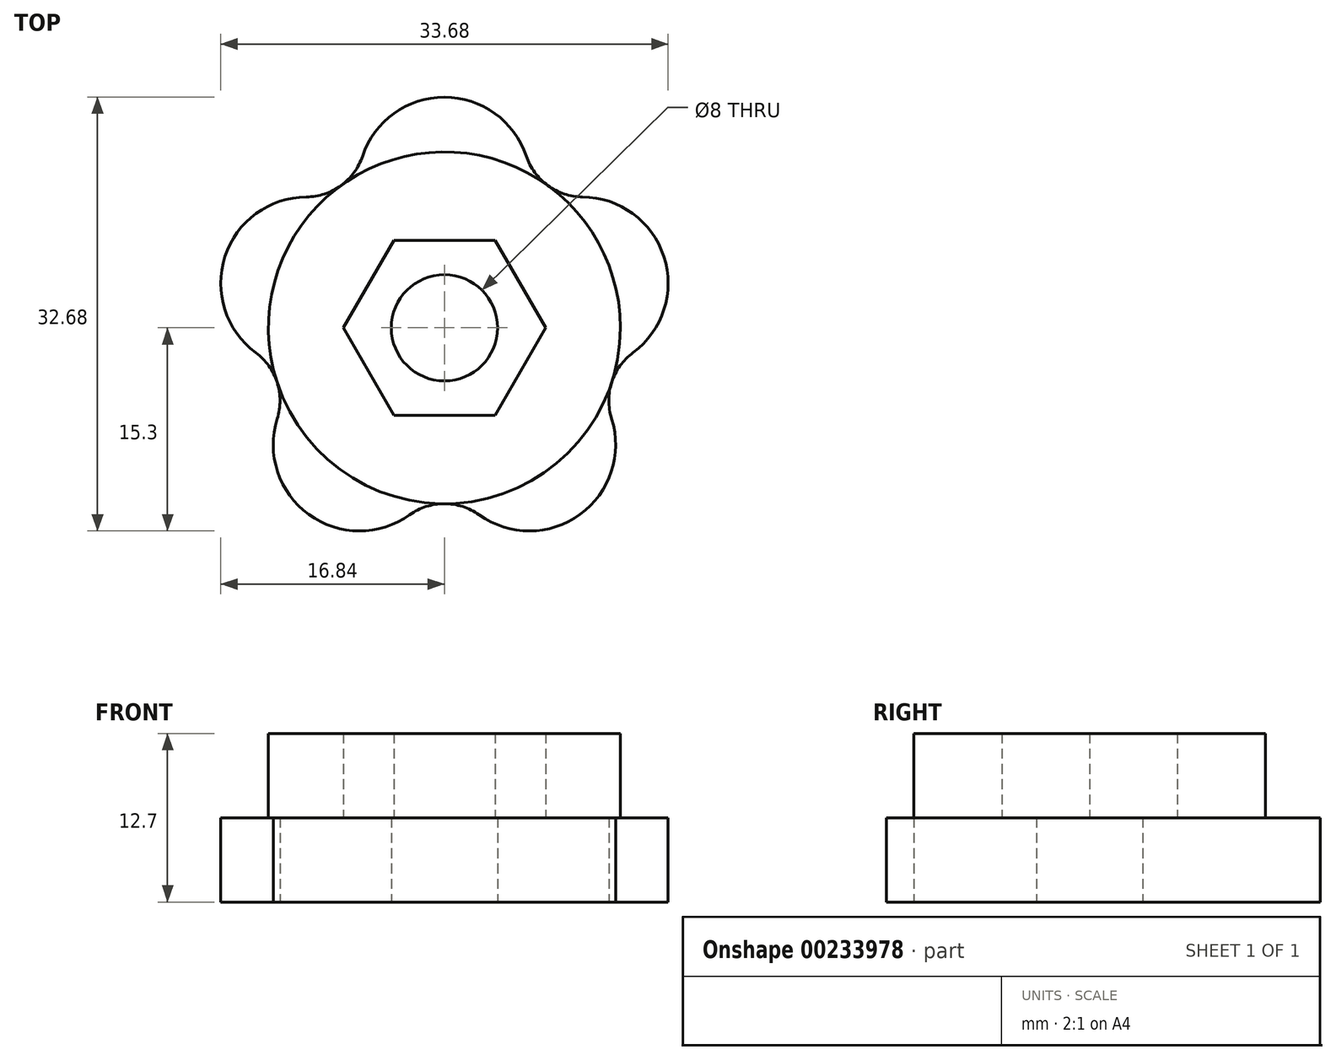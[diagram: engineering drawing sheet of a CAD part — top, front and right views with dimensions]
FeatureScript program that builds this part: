
annotation { "Feature Type Name" : "Feature", "Feature Type Description" : "" }
export const myFeature = defineFeature(function(context is Context, id is Id, definition is map)
    precondition{}
    {
        {
            var Q0;
            Q0=qCreatedBy(makeId("Top.planeOp"),FACE);
            var sketch = newSketch(context, id + "F0", { "sketchPlane" : qUnion([Q0])});
            skCircle(sketch, "E0", {"center": v(0, 0) * mm, "radius": 4 * mm});
            skArc(sketch, "E1", {"start": v(6.17, 12.93) * mm, "mid": v(0, 17.37) * mm, "end": v(-6.17, 12.93) * mm});
            skCircle(sketch, "E2", {"center": v(0, 0) * mm, "radius": 17.38 * mm, "construction": true});
            skArc(sketch, "E3.1.0", {"start": v(-10.4, 9.86) * mm, "mid": v(-16.52, 5.37) * mm, "end": v(-14.2, -1.87) * mm});
            skArc(sketch, "E3.2.0", {"start": v(-12.6, -6.84) * mm, "mid": v(-10.21, -14.06) * mm, "end": v(-2.61, -14.09) * mm});
            skArc(sketch, "E3.3.0", {"start": v(2.61, -14.09) * mm, "mid": v(10.21, -14.06) * mm, "end": v(12.6, -6.84) * mm});
            skArc(sketch, "E3.4.0", {"start": v(14.2, -1.87) * mm, "mid": v(16.52, 5.37) * mm, "end": v(10.4, 9.86) * mm});
            skLineSegment(sketch, "E4", {"start": v(0, 0) * mm, "end": v(-10.21, 14.06) * mm, "construction": true});
            skArc(sketch, "E5", {"start": v(-10.4, 9.86) * mm, "mid": v(-7.79, 10.72) * mm, "end": v(-6.17, 12.93) * mm});
            skArc(sketch, "E6.1.0", {"start": v(-12.6, -6.84) * mm, "mid": v(-12.6, -4.1) * mm, "end": v(-14.2, -1.87) * mm});
            skArc(sketch, "E6.2.0", {"start": v(2.61, -14.09) * mm, "mid": v(0, -13.25) * mm, "end": v(-2.61, -14.09) * mm});
            skArc(sketch, "E6.3.0", {"start": v(14.2, -1.87) * mm, "mid": v(12.6, -4.1) * mm, "end": v(12.6, -6.84) * mm});
            skArc(sketch, "E6.4.0", {"start": v(6.17, 12.93) * mm, "mid": v(7.79, 10.72) * mm, "end": v(10.4, 9.86) * mm});
            skSolve(sketch);
        }
        {
            var Q0;
            Q0=makeQuery(id+"F0.imprint","IMPRINT",FACE,{"disambiguationData":[TD([[makeQuery(id+"F0.imprint","IMPRINT",EDGE,{"derivedFrom":sQuery(id+"F0.wireOp",EDGE,"E0")}),-1.0]])]});
            extrude(context, id + "F1", {"entities" : qUnion([Q0]), "depth" : 6.35 * mm});
        }
        {
            var Q0;
            Q0=makeQuery(id+"F1.opExtrude","CAP_FACE",FACE,{"disambiguationData":[OSD([sQuery(id+"F0.wireOp",EDGE,"E0"),sQuery(id+"F0.wireOp",EDGE,"E1"),sQuery(id+"F0.wireOp",EDGE,"E3.1.0"),sQuery(id+"F0.wireOp",EDGE,"E3.2.0"),sQuery(id+"F0.wireOp",EDGE,"E3.3.0"),sQuery(id+"F0.wireOp",EDGE,"E3.4.0"),sQuery(id+"F0.wireOp",EDGE,"E5"),sQuery(id+"F0.wireOp",EDGE,"E6.1.0"),sQuery(id+"F0.wireOp",EDGE,"E6.2.0"),sQuery(id+"F0.wireOp",EDGE,"E6.3.0"),sQuery(id+"F0.wireOp",EDGE,"E6.4.0")])],"isStart":false});
            var sketch = newSketch(context, id + "F2", { "sketchPlane" : qUnion([Q0])});
            skCircle(sketch, "E7", {"center": v(0, 0) * mm, "radius": 13.25 * mm});
            skCircle(sketch, "E8.cCircle", {"center": v(0, 0) * mm, "radius": 6.6 * mm, "construction": true});
            skLineSegment(sketch, "E8.0", {"start": v(-3.81, 6.6) * mm, "end": v(3.81, 6.6) * mm});
            skLineSegment(sketch, "E8.1", {"start": v(3.81, 6.6) * mm, "end": v(7.62, 0) * mm});
            skLineSegment(sketch, "E8.2", {"start": v(7.62, 0) * mm, "end": v(3.81, -6.6) * mm});
            skLineSegment(sketch, "E8.3", {"start": v(3.81, -6.6) * mm, "end": v(-3.81, -6.6) * mm});
            skLineSegment(sketch, "E8.4", {"start": v(-3.81, -6.6) * mm, "end": v(-7.62, 0) * mm});
            skLineSegment(sketch, "E8.5", {"start": v(-7.62, 0) * mm, "end": v(-3.81, 6.6) * mm});
            skPoint(sketch, "E8.0.midPoint", {"position": v(0, 6.6) * mm});
            skSolve(sketch);
        }
        {
            var Q0;
            Q0=makeQuery(id+"F2.imprint","IMPRINT",FACE,{"disambiguationData":[TD([[makeQuery(id+"F2.imprint","IMPRINT",EDGE,{"derivedFrom":sQuery(id+"F2.wireOp",EDGE,"E8.0")}),1.0]])]});
            extrude(context, id + "F3", {"entities" : qUnion([Q0]), "operationType" : NewBodyOperationType.ADD, "depth" : 6.35 * mm});
        }
    });
